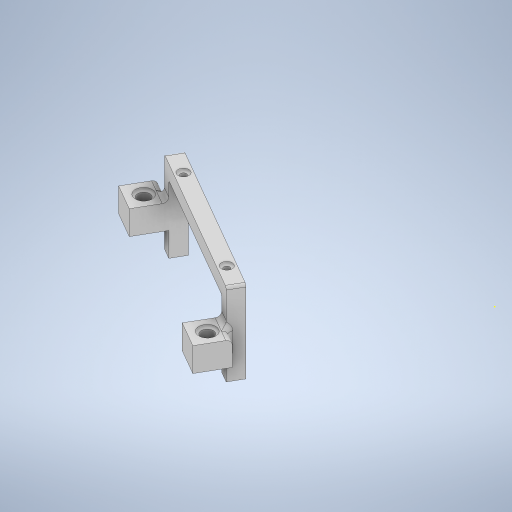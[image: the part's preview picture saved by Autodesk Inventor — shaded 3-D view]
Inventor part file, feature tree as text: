
AUTODESK INVENTOR PART (.ipt)
format: ipt  version: 2023 (Build 270158000, 158)  size: 763,392 bytes
history: native  units: mm
features: extrude x7, sketch x5, fillet x4, other x1
ambient origin geometry x8: Origin, YZ Plane, XZ Plane, XY Plane, X Axis, Y Axis, Z Axis, Center Point
bodies: Body1 (feature_tree)
feature tree (17):
  other  "Bryła1"
  sketch  "Szkic1"
  extrude  "Wyciągnięcie proste1"  Depth=8.0mm
  extrude  "Wyciągnięcie proste3"  Depth=34.0mm TaperAngle=0.0deg
  extrude  "Wyciągnięcie proste4"  Depth=6.0mm
  sketch  "Szkic5"
  extrude  "Wyciągnięcie proste5"  Depth=60.0mm TaperAngle=0.0deg
  extrude  "Wyciągnięcie proste6"  Depth=2.5mm
  extrude  "Wyciągnięcie proste7"  Depth=2.5mm
  extrude  "Wyciągnięcie proste8"  Depth=49.0mm
  fillet  "Zaokrąglenie1"  Radius=10.5mm
  fillet  "Zaokrąglenie2"  Radius=3.0mm
  fillet  "Zaokrąglenie3"  Radius=3.0mm
  fillet  "Zaokrąglenie4"  Radius=60.0mm
  sketch  "Szkic3"
  sketch  "Szkic4"
  sketch  "Szkic7"
